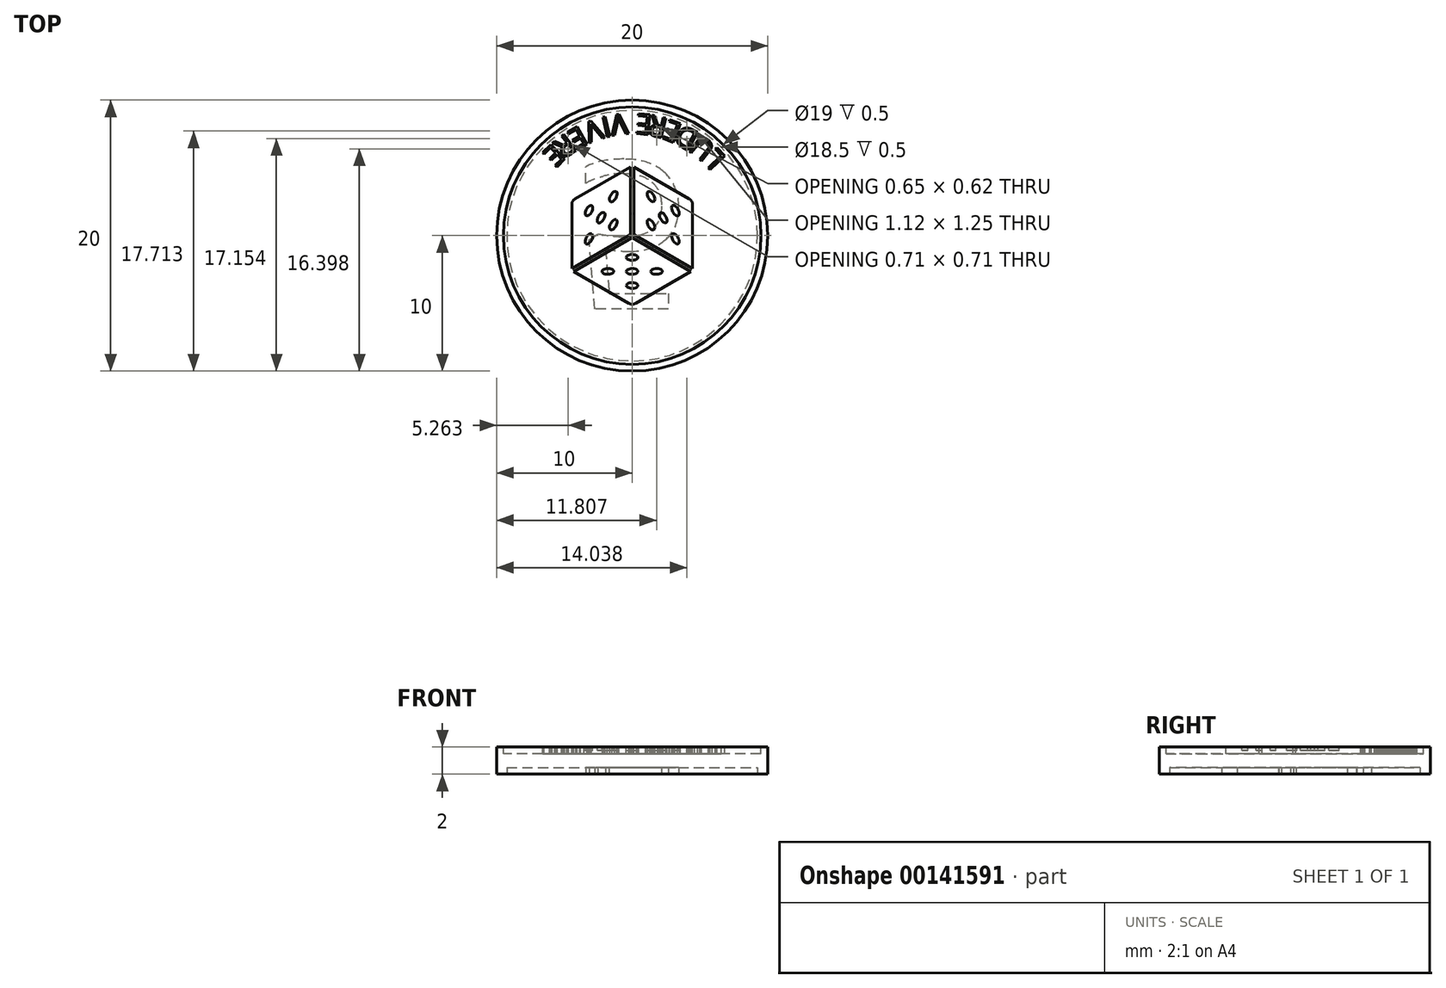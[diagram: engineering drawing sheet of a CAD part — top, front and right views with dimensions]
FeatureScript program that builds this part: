
annotation { "Feature Type Name" : "Feature", "Feature Type Description" : "" }
export const myFeature = defineFeature(function(context is Context, id is Id, definition is map)
    precondition{}
    {
        {
            var Q0;
            Q0=qCreatedBy(makeId("Top.planeOp"),FACE);
            var sketch = newSketch(context, id + "F0", { "sketchPlane" : qUnion([Q0])});
            skCircle(sketch, "E0", {"center": v(0, 0) * mm, "radius": 10 * mm});
            skSolve(sketch);
        }
        {
            var Q0;
            Q0 = qSketchRegion(id + "F0", true);
            extrude(context, id + "F1", {"entities" : qUnion([Q0]), "depth" : 2 * mm});
        }
        {
            var Q0;
            Q0=makeQuery(id+"F1.opExtrude","CAP_FACE",FACE,{"disambiguationData":[OSD([sQuery(id+"F0.wireOp",EDGE,"E0")])],"isStart":false});
            var sketch = newSketch(context, id + "F2", { "sketchPlane" : qUnion([Q0])});
            skCircle(sketch, "E1.0", {"center": v(0, 0) * mm, "radius": 9.5 * mm});
            skSolve(sketch);
        }
        {
            var Q0;
            Q0 = qSketchRegion(id + "F2", true);
            extrude(context, id + "F3", {"entities" : qUnion([Q0]), "operationType" : NewBodyOperationType.REMOVE, "oppositeDirection" : true, "depth" : 0.5 * mm});
        }
        {
            var Q0;
            Q0=makeQuery(id+"F1.opExtrude","CAP_FACE",FACE,{"disambiguationData":[OSD([sQuery(id+"F0.wireOp",EDGE,"E0")])],"isStart":true});
            var sketch = newSketch(context, id + "F4", { "sketchPlane" : qUnion([Q0])});
            skCircle(sketch, "E2.0", {"center": v(0, 0) * mm, "radius": 9.25 * mm});
            skSolve(sketch);
        }
        {
            var Q0;
            Q0 = qSketchRegion(id + "F4", true);
            extrude(context, id + "F5", {"entities" : qUnion([Q0]), "operationType" : NewBodyOperationType.REMOVE, "oppositeDirection" : true, "depth" : 0.5 * mm});
        }
        {
            var Q0;
            Q0=makeQuery(id+"F2.imprint","IMPRINT",FACE,{"disambiguationData":[TD([[makeQuery(id+"F2.imprint","IMPRINT",EDGE,{"derivedFrom":sQuery(id+"F2.wireOp",EDGE,"E1.0")}),1.0]])]});
            var sketch = newSketch(context, id + "F6", { "sketchPlane" : qUnion([Q0])});
            skLineSegment(sketch, "E3", {"start": v(0, 0) * mm, "end": v(0, 9.5) * mm, "construction": true});
            skLineSegment(sketch, "E4", {"start": v(0, 0) * mm, "end": v(-8.23, -4.75) * mm, "construction": true});
            skLineSegment(sketch, "E5", {"start": v(0, 0) * mm, "end": v(8.23, -4.75) * mm, "construction": true});
            skCircle(sketch, "E6", {"center": v(0, 0) * mm, "radius": 9.5 * mm, "construction": true});
            skLineSegment(sketch, "E7", {"start": v(-0.13, 5.07) * mm, "end": v(-0.12, 0.07) * mm});
            skLineSegment(sketch, "E8", {"start": v(-0.12, 0.07) * mm, "end": v(-4.46, -2.43) * mm});
            skLineSegment(sketch, "E9", {"start": v(-4.46, -2.43) * mm, "end": v(-4.46, 2.28) * mm});
            skLineSegment(sketch, "E10", {"start": v(-4.2, 2.72) * mm, "end": v(-0.13, 5.07) * mm});
            skPoint(sketch, "E11.visualSharp", {"position": v(-4.46, 2.57) * mm});
            skArc(sketch, "E11.filletArc", {"start": v(-4.2, 2.72) * mm, "mid": v(-4.39, 2.53) * mm, "end": v(-4.46, 2.28) * mm});
            skPoint(sketch, "E12.1.1", {"position": v(0, -5.14) * mm});
            skLineSegment(sketch, "E12.1.3", {"start": v(-4.33, -2.64) * mm, "end": v(0, -0.14) * mm});
            skLineSegment(sketch, "E12.1.5", {"start": v(0, -0.14) * mm, "end": v(4.33, -2.64) * mm});
            skLineSegment(sketch, "E12.1.6", {"start": v(4.33, -2.64) * mm, "end": v(0.25, -5) * mm});
            skLineSegment(sketch, "E12.1.7", {"start": v(-0.25, -5) * mm, "end": v(-4.33, -2.64) * mm});
            skArc(sketch, "E12.1.8", {"start": v(-0.25, -5) * mm, "mid": v(0, -5.07) * mm, "end": v(0.25, -5) * mm});
            skPoint(sketch, "E12.2.1", {"position": v(4.46, 2.57) * mm});
            skLineSegment(sketch, "E12.2.3", {"start": v(4.46, -2.43) * mm, "end": v(0.13, 0.07) * mm});
            skLineSegment(sketch, "E12.2.5", {"start": v(0.12, 0.07) * mm, "end": v(0.13, 5.07) * mm});
            skLineSegment(sketch, "E12.2.6", {"start": v(0.13, 5.07) * mm, "end": v(4.2, 2.72) * mm});
            skLineSegment(sketch, "E12.2.7", {"start": v(4.46, 2.28) * mm, "end": v(4.46, -2.43) * mm});
            skArc(sketch, "E12.2.8", {"start": v(4.46, 2.28) * mm, "mid": v(4.39, 2.53) * mm, "end": v(4.2, 2.72) * mm});
            skSolve(sketch);
        }
        {
            var Q0;
            Q0 = qSketchRegion(id + "F6", true);
            extrude(context, id + "F7", {"entities" : qUnion([Q0]), "operationType" : NewBodyOperationType.ADD, "endBound" : BoundingType.UP_TO_NEXT, "oppositeDirection" : true, "depth" : 25 * mm});
        }
        {
            var Q0;
            Q0=makeQuery(id+"F7.opExtrude","CAP_FACE",FACE,{"disambiguationData":[OSD([sQuery(id+"F6.wireOp",EDGE,"E12.1.3"),sQuery(id+"F6.wireOp",EDGE,"E12.1.5"),sQuery(id+"F6.wireOp",EDGE,"E12.1.6"),sQuery(id+"F6.wireOp",EDGE,"E12.1.7"),sQuery(id+"F6.wireOp",EDGE,"E12.1.8")])],"isStart":true});
            var sketch = newSketch(context, id + "F8", { "sketchPlane" : qUnion([Q0])});
            skLineSegment(sketch, "E13", {"start": v(-4.33, -2.64) * mm, "end": v(4.33, -2.64) * mm, "construction": true});
            skLineSegment(sketch, "E14", {"start": v(0, -0.14) * mm, "end": v(0, -5.07) * mm, "construction": true});
            skLineSegment(sketch, "E15", {"start": v(-0.56, -2.64) * mm, "end": v(0, -2.32) * mm, "construction": true});
            skLineSegment(sketch, "E16", {"start": v(0, -2.32) * mm, "end": v(0.56, -2.64) * mm, "construction": true});
            skLineSegment(sketch, "E17", {"start": v(0.56, -2.64) * mm, "end": v(0, -2.97) * mm, "construction": true});
            skLineSegment(sketch, "E18", {"start": v(0, -2.97) * mm, "end": v(-0.56, -2.64) * mm, "construction": true});
            skLineSegment(sketch, "E19", {"start": v(-0.28, -2.48) * mm, "end": v(0.28, -2.8) * mm, "construction": true});
            skLineSegment(sketch, "E20", {"start": v(-0.28, -2.8) * mm, "end": v(0.28, -2.48) * mm, "construction": true});
            skEllipse(sketch, "E21", {"center": v(0, -2.64) * mm, "majorRadius": 0.43 * mm, "minorRadius": 0.22 * mm, "majorAxis": v(-1, 0)});
            skEllipse(sketch, "E22.1.0.0", {"center": v(1.8, -2.64) * mm, "majorRadius": 0.43 * mm, "minorRadius": 0.22 * mm, "majorAxis": v(-1, 0)});
            skLineSegment(sketch, "E22.direction1", {"start": v(0, -2.64) * mm, "end": v(1.8, -2.64) * mm, "construction": true});
            skEllipse(sketch, "E23.1.0.0", {"center": v(-1.8, -2.64) * mm, "majorRadius": 0.43 * mm, "minorRadius": 0.22 * mm, "majorAxis": v(-1, 0)});
            skLineSegment(sketch, "E23.direction1", {"start": v(0, -2.64) * mm, "end": v(-1.8, -2.64) * mm, "construction": true});
            skEllipse(sketch, "E24.1.0.0", {"center": v(0, -3.68) * mm, "majorRadius": 0.43 * mm, "minorRadius": 0.22 * mm, "majorAxis": v(-1, 0)});
            skLineSegment(sketch, "E24.direction1", {"start": v(0, -2.64) * mm, "end": v(0, -3.68) * mm, "construction": true});
            skLineSegment(sketch, "E25", {"start": v(0, -3.68) * mm, "end": v(1.8, -2.64) * mm, "construction": true});
            skEllipse(sketch, "E26.1.0.0", {"center": v(0, -1.6) * mm, "majorRadius": 0.43 * mm, "minorRadius": 0.22 * mm, "majorAxis": v(-1, 0)});
            skLineSegment(sketch, "E26.direction1", {"start": v(0, -2.64) * mm, "end": v(0, -1.6) * mm, "construction": true});
            skLineSegment(sketch, "E27", {"start": v(-1.8, -2.64) * mm, "end": v(0, -1.6) * mm});
            skLineSegment(sketch, "E28.1.0", {"start": v(2.3, 1.32) * mm, "end": v(3.2, -0.24) * mm, "construction": true});
            skLineSegment(sketch, "E28.1.1", {"start": v(3.2, -0.24) * mm, "end": v(1.4, 0.8) * mm});
            skEllipse(sketch, "E28.1.2", {"center": v(1.4, 0.8) * mm, "majorRadius": 0.43 * mm, "minorRadius": 0.22 * mm, "majorAxis": v(0.5, -0.87)});
            skEllipse(sketch, "E28.1.3", {"center": v(1.4, 2.88) * mm, "majorRadius": 0.43 * mm, "minorRadius": 0.22 * mm, "majorAxis": v(0.5, -0.87)});
            skLineSegment(sketch, "E28.1.4", {"start": v(2.3, 1.32) * mm, "end": v(1.4, 2.88) * mm, "construction": true});
            skEllipse(sketch, "E28.1.5", {"center": v(3.2, -0.24) * mm, "majorRadius": 0.43 * mm, "minorRadius": 0.22 * mm, "majorAxis": v(0.5, -0.87)});
            skLineSegment(sketch, "E28.1.6", {"start": v(2.3, 1.32) * mm, "end": v(1.4, 0.8) * mm, "construction": true});
            skEllipse(sketch, "E28.1.7", {"center": v(3.2, 1.84) * mm, "majorRadius": 0.43 * mm, "minorRadius": 0.22 * mm, "majorAxis": v(0.5, -0.87)});
            skLineSegment(sketch, "E28.1.8", {"start": v(4.46, -2.43) * mm, "end": v(0.12, 5.07) * mm, "construction": true});
            skLineSegment(sketch, "E28.1.9", {"start": v(0.12, 0.07) * mm, "end": v(4.39, 2.53) * mm, "construction": true});
            skLineSegment(sketch, "E28.1.10", {"start": v(3.2, 1.84) * mm, "end": v(1.4, 2.88) * mm, "construction": true});
            skLineSegment(sketch, "E28.1.11", {"start": v(2.3, 1.32) * mm, "end": v(3.2, 1.84) * mm, "construction": true});
            skEllipse(sketch, "E28.1.12", {"center": v(2.3, 1.32) * mm, "majorRadius": 0.43 * mm, "minorRadius": 0.22 * mm, "majorAxis": v(0.5, -0.87)});
            skLineSegment(sketch, "E28.1.13", {"start": v(2.57, 1.16) * mm, "end": v(2, 1.48) * mm, "construction": true});
            skLineSegment(sketch, "E28.1.14", {"start": v(2.3, 1) * mm, "end": v(2.3, 1.65) * mm, "construction": true});
            skLineSegment(sketch, "E28.1.15", {"start": v(2, 1.8) * mm, "end": v(2.57, 1.48) * mm, "construction": true});
            skLineSegment(sketch, "E28.1.16", {"start": v(2.57, 1.48) * mm, "end": v(2.57, 0.83) * mm, "construction": true});
            skLineSegment(sketch, "E28.1.17", {"start": v(2, 1.16) * mm, "end": v(2, 1.8) * mm, "construction": true});
            skLineSegment(sketch, "E28.1.18", {"start": v(2.57, 0.83) * mm, "end": v(2, 1.16) * mm, "construction": true});
            skLineSegment(sketch, "E28.2.0", {"start": v(-2.3, 1.32) * mm, "end": v(-1.4, 2.88) * mm, "construction": true});
            skLineSegment(sketch, "E28.2.1", {"start": v(-1.4, 2.88) * mm, "end": v(-1.4, 0.8) * mm});
            skEllipse(sketch, "E28.2.2", {"center": v(-1.4, 0.8) * mm, "majorRadius": 0.43 * mm, "minorRadius": 0.22 * mm, "majorAxis": v(0.5, 0.87)});
            skEllipse(sketch, "E28.2.3", {"center": v(-3.2, -0.24) * mm, "majorRadius": 0.43 * mm, "minorRadius": 0.22 * mm, "majorAxis": v(0.5, 0.87)});
            skLineSegment(sketch, "E28.2.4", {"start": v(-2.3, 1.32) * mm, "end": v(-3.2, -0.24) * mm, "construction": true});
            skEllipse(sketch, "E28.2.5", {"center": v(-1.4, 2.88) * mm, "majorRadius": 0.43 * mm, "minorRadius": 0.22 * mm, "majorAxis": v(0.5, 0.87)});
            skLineSegment(sketch, "E28.2.6", {"start": v(-2.3, 1.32) * mm, "end": v(-1.4, 0.8) * mm, "construction": true});
            skEllipse(sketch, "E28.2.7", {"center": v(-3.2, 1.84) * mm, "majorRadius": 0.43 * mm, "minorRadius": 0.22 * mm, "majorAxis": v(0.5, 0.87)});
            skLineSegment(sketch, "E28.2.8", {"start": v(-0.12, 5.07) * mm, "end": v(-4.46, -2.43) * mm, "construction": true});
            skLineSegment(sketch, "E28.2.9", {"start": v(-0.12, 0.07) * mm, "end": v(-4.39, 2.53) * mm, "construction": true});
            skLineSegment(sketch, "E28.2.10", {"start": v(-3.2, 1.84) * mm, "end": v(-3.2, -0.24) * mm, "construction": true});
            skLineSegment(sketch, "E28.2.11", {"start": v(-2.3, 1.32) * mm, "end": v(-3.2, 1.84) * mm, "construction": true});
            skEllipse(sketch, "E28.2.12", {"center": v(-2.3, 1.32) * mm, "majorRadius": 0.43 * mm, "minorRadius": 0.22 * mm, "majorAxis": v(0.5, 0.87)});
            skLineSegment(sketch, "E28.2.13", {"start": v(-2.3, 1.65) * mm, "end": v(-2.3, 1) * mm, "construction": true});
            skLineSegment(sketch, "E28.2.14", {"start": v(-2, 1.48) * mm, "end": v(-2.57, 1.16) * mm, "construction": true});
            skLineSegment(sketch, "E28.2.15", {"start": v(-2.57, 0.83) * mm, "end": v(-2.57, 1.48) * mm, "construction": true});
            skLineSegment(sketch, "E28.2.16", {"start": v(-2.57, 1.48) * mm, "end": v(-2, 1.8) * mm, "construction": true});
            skLineSegment(sketch, "E28.2.17", {"start": v(-2, 1.16) * mm, "end": v(-2.57, 0.83) * mm, "construction": true});
            skLineSegment(sketch, "E28.2.18", {"start": v(-2, 1.8) * mm, "end": v(-2, 1.16) * mm, "construction": true});
            skPoint(sketch, "E28.center", {"position": v(0, 0) * mm});
            skCircle(sketch, "E29", {"center": v(0, 0) * mm, "radius": 9 * mm, "construction": true});
            skSolve(sketch);
        }
        {
            var Q0;
            Q0 = qSketchRegion(id + "F8", true);
            extrude(context, id + "F9", {"entities" : qUnion([Q0]), "operationType" : NewBodyOperationType.REMOVE, "oppositeDirection" : true, "depth" : 0.25 * mm});
        }
        {
            var Q0;
            Q0=makeQuery(id+"F7.opExtrude","CAP_FACE",FACE,{"disambiguationData":[OSD([sQuery(id+"F6.wireOp",EDGE,"E12.2.3"),sQuery(id+"F6.wireOp",EDGE,"E12.2.5"),sQuery(id+"F6.wireOp",EDGE,"E12.2.6"),sQuery(id+"F6.wireOp",EDGE,"E12.2.7"),sQuery(id+"F6.wireOp",EDGE,"E12.2.8")])],"isStart":true});
            var sketch = newSketch(context, id + "F10", { "sketchPlane" : qUnion([Q0])});
            skCircle(sketch, "E30", {"center": v(0, 0) * mm, "radius": 9 * mm, "construction": true});
            skLineSegment(sketch, "E31", {"start": v(0, 0) * mm, "end": v(0.12, 9) * mm, "construction": true});
            skText(sketch, "E32", { "text": "E", "fontName": "OpenSans-Regular.ttf"});
            skText(sketch, "E33", { "text": "L", "fontName": "OpenSans-Regular.ttf"});
            skText(sketch, "E34", { "text": "U", "fontName": "OpenSans-Regular.ttf"});
            skText(sketch, "E35", { "text": "D", "fontName": "OpenSans-Regular.ttf"});
            skText(sketch, "E36", { "text": "E", "fontName": "OpenSans-Regular.ttf"});
            skText(sketch, "E37", { "text": "R", "fontName": "OpenSans-Regular.ttf"});
            skText(sketch, "E38", { "text": "V", "fontName": "OpenSans-Regular.ttf"});
            skText(sketch, "E39", { "text": "I", "fontName": "OpenSans-Regular.ttf"});
            skText(sketch, "E40", { "text": "V", "fontName": "OpenSans-Regular.ttf"});
            skText(sketch, "E41", { "text": "E", "fontName": "OpenSans-Regular.ttf"});
            skText(sketch, "E42", { "text": "R", "fontName": "OpenSans-Regular.ttf"});
            skText(sketch, "E43", { "text": "E", "fontName": "OpenSans-Regular.ttf"});
            const initialGuessF10  = {"E32": [0.0015, 0.0089, -0.99489, 0.10098, 0.0015], "E33": [0.00696, 0.00574, -0.6846, 0.72892, 0.0015], "E34": [0.0062, 0.00656, -0.77938, 0.62655, 0.0015], "E35": [0.005, 0.00752, -0.87634, 0.48169, 0.0015], "E36": [0.00374, 0.0082, -0.93485, 0.35504, 0.0015], "E37": [0.00267, 0.00862, -0.97517, 0.22148, 0.0015], "E38": [-0.00045, 0.00902, -0.9921, -0.1254, 0.0015], "E39": [-0.0018, 0.00882, -0.97356, -0.22842, 0.0015], "E40": [-0.00254, 0.00866, -0.93542, -0.35354, 0.0015], "E41": [-0.00388, 0.00814, -0.87289, -0.48792, 0.0015], "E42": [-0.00489, 0.00759, -0.79649, -0.60466, 0.0015], "E43": [-0.00586, 0.00686, -0.71686, -0.69722, 0.0015]};
            skSetInitialGuess(sketch, initialGuessF10);
            skSolve(sketch);
        }
        {
            var Q0;
            Q0 = qSketchRegion(id + "F10", true);
            var Q1;
            Q1=makeQuery(id+"F7.opExtrude","CAP_FACE",FACE,{"disambiguationData":[OSD([sQuery(id+"F6.wireOp",EDGE,"E12.2.3"),sQuery(id+"F6.wireOp",EDGE,"E12.2.5"),sQuery(id+"F6.wireOp",EDGE,"E12.2.6"),sQuery(id+"F6.wireOp",EDGE,"E12.2.7"),sQuery(id+"F6.wireOp",EDGE,"E12.2.8")])],"isStart":true});
            extrude(context, id + "F11", {"entities" : qUnion([Q0]), "endBound" : BoundingType.UP_TO_NEXT, "oppositeDirection" : true, "endBoundEntityFace" : qUnion([Q1]), "depth" : 25 * mm});
        }
        {
            var Q0;
            Q0=makeQuery(id+"F4.imprint","IMPRINT",FACE,{"disambiguationData":[TD([[makeQuery(id+"F4.imprint","IMPRINT",EDGE,{"derivedFrom":sQuery(id+"F4.wireOp",EDGE,"E2.0")}),-1.0]])]});
            cPlane(context, id + "F12", {"entities" : qUnion([Q0]), "cplaneType" : CPlaneType.OFFSET, "offset" : 0 * mm, "width" : 150 * mm, "height" : 150 * mm});
        }
        {
            var Q0;
            Q0=qCreatedBy(id+"F12.planeOp",FACE);
            var sketch = newSketch(context, id + "F13", { "sketchPlane" : qUnion([Q0])});
            skText(sketch, "E44", { "text": "5", "fontName": "OpenSans-Regular.ttf"});
            skPoint(sketch, "E45", {"position": v(0, 0) * mm});
            const initialGuessF13  = {"E44": [-0.00442, -0.0055, 1, 0, 0.011]};
            skSetInitialGuess(sketch, initialGuessF13);
            skSolve(sketch);
        }
        {
            var Q0;
            Q0 = qSketchRegion(id + "F13", true);
            extrude(context, id + "F14", {"entities" : qUnion([Q0]), "endBound" : BoundingType.UP_TO_NEXT, "oppositeDirection" : true, "depth" : 25 * mm});
        }
    });
